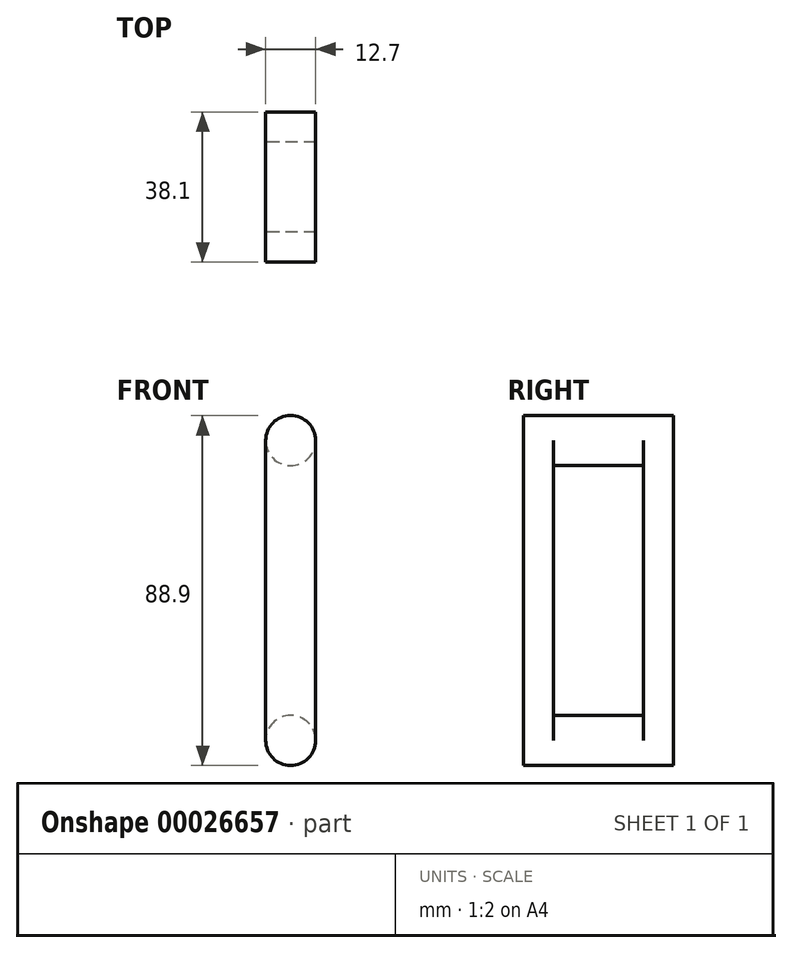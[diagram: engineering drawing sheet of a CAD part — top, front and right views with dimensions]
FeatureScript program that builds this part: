
annotation { "Feature Type Name" : "Feature", "Feature Type Description" : "" }
export const myFeature = defineFeature(function(context is Context, id is Id, definition is map)
    precondition{}
    {
        {
            var Q0;
            Q0=qCreatedBy(makeId("Front.planeOp"),FACE);
            var sketch = newSketch(context, id + "F0", { "sketchPlane" : qUnion([Q0])});
            skCircle(sketch, "E0", {"center": v(-44.1, 14.15) * mm, "radius": 6.35 * mm});
            skSolve(sketch);
        }
        {
            var Q0;
            Q0 = qSketchRegion(id + "F0", true);
            extrude(context, id + "F1", {"entities" : qUnion([Q0]), "depth" : 19.05 * mm});
        }
        {
            var Q0;
            Q0=makeQuery(id+"F1.opExtrude","CAP_FACE",FACE,{"disambiguationData":[OSD([sQuery(id+"F0.wireOp",EDGE,"E0")])],"isStart":false});
            var sketch = newSketch(context, id + "F2", { "sketchPlane" : qUnion([Q0])});
            skCircle(sketch, "E1", {"center": v(-44.1, 90.35) * mm, "radius": 6.35 * mm});
            skLineSegment(sketch, "E2", {"start": v(-50.45, 90.35) * mm, "end": v(-50.45, 14.15) * mm});
            skLineSegment(sketch, "E3", {"start": v(-50.45, 14.15) * mm, "end": v(-37.75, 14.15) * mm});
            skLineSegment(sketch, "E4", {"start": v(-50.45, 90.35) * mm, "end": v(-37.75, 90.35) * mm});
            skLineSegment(sketch, "E5", {"start": v(-37.75, 14.15) * mm, "end": v(-37.75, 90.35) * mm});
            skSolve(sketch);
        }
        {
            var Q0;
            {var subQ3=sQuery(id+"F2.wireOp",EDGE,"E2");Q0=makeQuery(id+"F2.imprint","IMPRINT",FACE,{"disambiguationData":[TD([[makeQuery(id+"F2.imprint","IMPRINT",EDGE,{"derivedFrom":subQ3}),1.0]])]});}
            extrude(context, id + "F3", {"entities" : qUnion([Q0]), "operationType" : NewBodyOperationType.ADD, "oppositeDirection" : true, "depth" : 7.62 * mm});
        }
        {
            var Q0;
            {var subQ0=sQuery(id+"F2.wireOp",EDGE,"E4");Q0=makeQuery(id+"F2.imprint","IMPRINT",FACE,{"disambiguationData":[TD([[makeQuery(id+"F2.imprint","IMPRINT",EDGE,{"derivedFrom":subQ0}),1.0]])]});}
            var Q1;
            {var subQ0=sQuery(id+"F2.wireOp",EDGE,"E4");Q1=makeQuery(id+"F2.imprint","IMPRINT",FACE,{"disambiguationData":[TD([[makeQuery(id+"F2.imprint","IMPRINT",EDGE,{"derivedFrom":subQ0}),-1.0]])]});}
            extrude(context, id + "F4", {"entities" : qUnion([Q0, Q1]), "operationType" : NewBodyOperationType.ADD, "oppositeDirection" : true, "depth" : 19.05 * mm});
        }
        {
            var Q0;
            Q0=makeQuery(id+"F1.opExtrude","SWEPT_BODY",BODY,{"disambiguationData":[OSD([sQuery(id+"F0.wireOp",EDGE,"E0")])]});
            var Q1;
            Q1=makeQuery(id+"F4.opExtrude","CAP_FACE",FACE,{"disambiguationData":[OSD([sQuery(id+"F2.wireOp",EDGE,"E1")])],"isStart":false});
            mirror(context, id + "F5", {"operationType" : NewBodyOperationType.ADD, "entities" : qUnion([Q0]), "mirrorPlane" : qUnion([Q1])});
        }
    });
